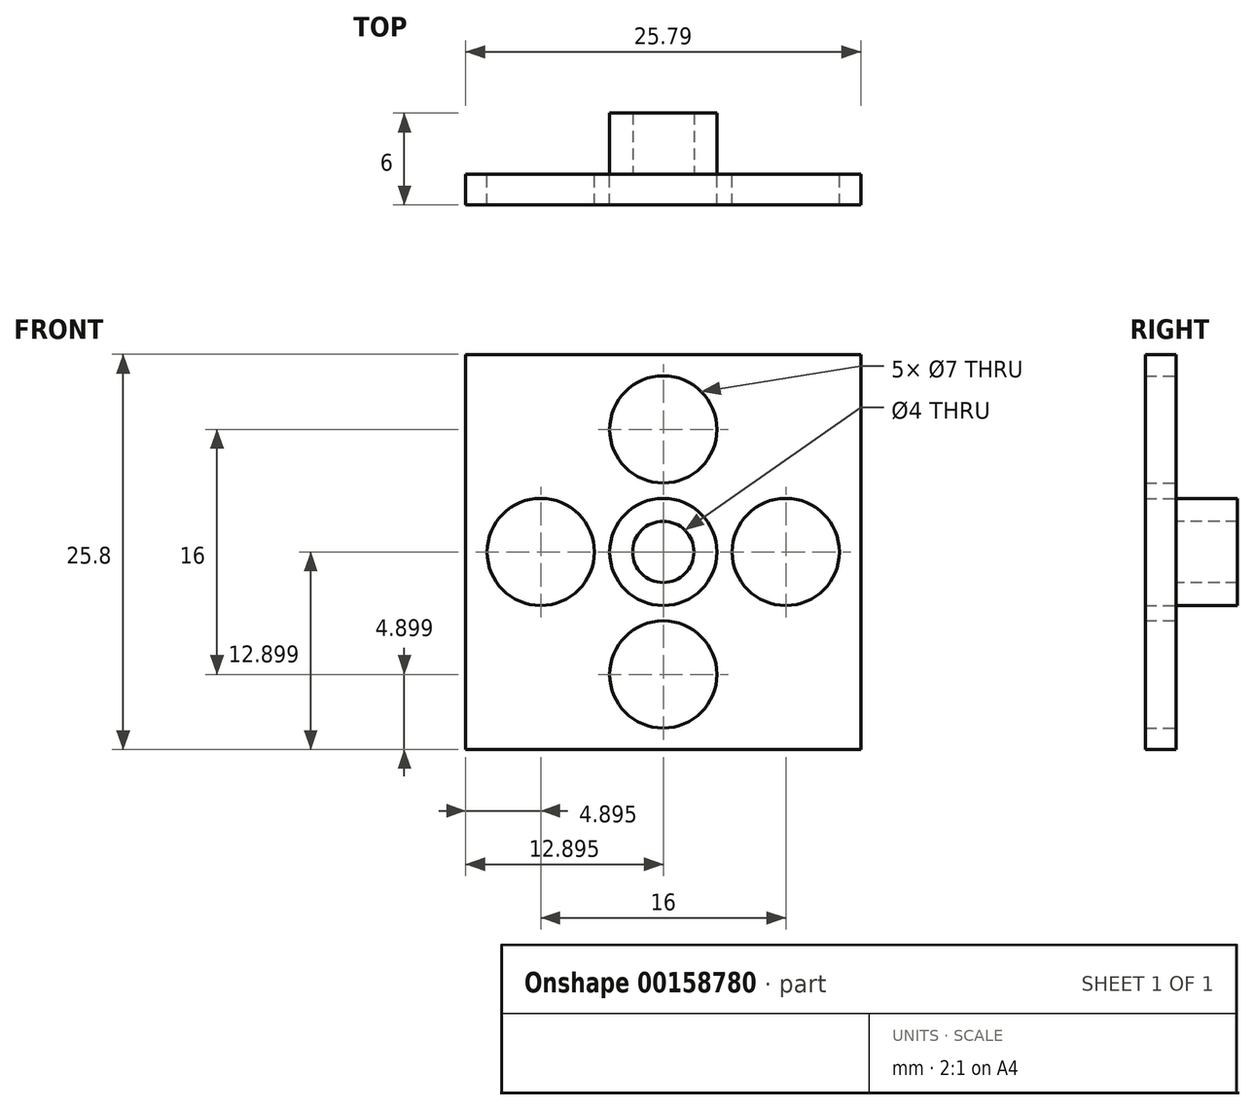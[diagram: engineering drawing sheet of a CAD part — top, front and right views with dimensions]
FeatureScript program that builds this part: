
annotation { "Feature Type Name" : "Feature", "Feature Type Description" : "" }
export const myFeature = defineFeature(function(context is Context, id is Id, definition is map)
    precondition{}
    {
        {
            var Q0;
            Q0=qCreatedBy(makeId("Front.planeOp"),FACE);
            var sketch = newSketch(context, id + "F0", { "sketchPlane" : qUnion([Q0])});
            skPoint(sketch, "E0.middle", {"position": v(0.36, -0.48) * mm});
            skLineSegment(sketch, "E1.top", {"start": v(-7.64, -8.48) * mm, "end": v(8.36, -8.48) * mm, "construction": true});
            skLineSegment(sketch, "E1.left", {"start": v(-7.64, 7.52) * mm, "end": v(-7.64, -8.48) * mm, "construction": true});
            skLineSegment(sketch, "E1.right", {"start": v(8.36, 7.52) * mm, "end": v(8.36, -8.48) * mm, "construction": true});
            skLineSegment(sketch, "E2", {"start": v(-7.64, 7.52) * mm, "end": v(8.36, 7.52) * mm, "construction": true});
            skLineSegment(sketch, "E3", {"start": v(0.36, -0.48) * mm, "end": v(-27.14, 27.02) * mm, "construction": true});
            skLineSegment(sketch, "E4", {"start": v(0.36, -0.48) * mm, "end": v(-27.14, -27.98) * mm, "construction": true});
            skLineSegment(sketch, "E5", {"start": v(0.36, -0.48) * mm, "end": v(27.86, 27.02) * mm, "construction": true});
            skLineSegment(sketch, "E6", {"start": v(0.36, -0.48) * mm, "end": v(27.86, -27.98) * mm, "construction": true});
            skLineSegment(sketch, "E7", {"start": v(0.36, -0.48) * mm, "end": v(0.36, 27.02) * mm, "construction": true});
            skLineSegment(sketch, "E8", {"start": v(0.36, -8.48) * mm, "end": v(0.36, -27.98) * mm, "construction": true});
            skPoint(sketch, "E9", {"position": v(-7.64, 7.52) * mm});
            skLineSegment(sketch, "E10", {"start": v(21.88, 21.04) * mm, "end": v(-21.17, 21.04) * mm, "construction": true});
            skLineSegment(sketch, "E11", {"start": v(-21.17, 21.04) * mm, "end": v(-21.17, -22) * mm, "construction": true});
            skLineSegment(sketch, "E12", {"start": v(-21.17, -22) * mm, "end": v(21.88, -22) * mm, "construction": true});
            skLineSegment(sketch, "E13", {"start": v(21.88, -22) * mm, "end": v(21.88, 21.04) * mm, "construction": true});
            skLineSegment(sketch, "E14", {"start": v(0.36, -0.48) * mm, "end": v(-19.04, -0.48) * mm, "construction": true});
            skLineSegment(sketch, "E15", {"start": v(-27.14, -0.48) * mm, "end": v(-19.04, -0.48) * mm, "construction": true});
            skLineSegment(sketch, "E16", {"start": v(0.36, -0.48) * mm, "end": v(27.86, -0.48) * mm, "construction": true});
            skLineSegment(sketch, "E17", {"start": v(0.36, -0.48) * mm, "end": v(0.36, -8.48) * mm, "construction": true});
            skCircle(sketch, "E18", {"center": v(8.36, -0.48) * mm, "radius": 1.5 * mm});
            skCircle(sketch, "E19", {"center": v(-7.64, -0.48) * mm, "radius": 1.5 * mm});
            skCircle(sketch, "E20", {"center": v(0.36, -8.48) * mm, "radius": 1.5 * mm});
            skLineSegment(sketch, "E21.MirrorCS", {"start": v(0.36, -0.48) * mm, "end": v(19.75, -0.48) * mm, "construction": true});
            skCircle(sketch, "E22", {"center": v(0.36, -0.48) * mm, "radius": 19.53 * mm, "construction": true});
            skLineSegment(sketch, "E23", {"start": v(0.36, 23.08) * mm, "end": v(0.36, 22.48) * mm});
            skCircle(sketch, "E24", {"center": v(0.36, -0.48) * mm, "radius": 2 * mm});
            skCircle(sketch, "E25", {"center": v(0.36, -0.48) * mm, "radius": 3.5 * mm});
            skCircle(sketch, "E26", {"center": v(0.36, -0.48) * mm, "radius": 4.9 * mm, "construction": true});
            skCircle(sketch, "E27", {"center": v(8.36, -0.48) * mm, "radius": 3.5 * mm});
            skLineSegment(sketch, "E28.bottom", {"start": v(-12.54, -13.38) * mm, "end": v(13.25, -13.38) * mm});
            skLineSegment(sketch, "E28.top", {"start": v(-12.54, 12.42) * mm, "end": v(13.25, 12.42) * mm});
            skLineSegment(sketch, "E28.left", {"start": v(-12.54, -13.38) * mm, "end": v(-12.54, 12.42) * mm});
            skLineSegment(sketch, "E28.right", {"start": v(13.25, -13.38) * mm, "end": v(13.25, 12.42) * mm});
            skCircle(sketch, "E29.MirrorC", {"center": v(-7.64, -0.48) * mm, "radius": 3.5 * mm});
            skCircle(sketch, "E30.MirrorC", {"center": v(0.36, -8.48) * mm, "radius": 3.5 * mm});
            skCircle(sketch, "E31.MirrorC", {"center": v(0.36, 7.52) * mm, "radius": 3.5 * mm});
            skSolve(sketch);
        }
        {
            var Q0;
            Q0=makeQuery(id+"F0.imprint","IMPRINT",FACE,{"disambiguationData":[TD([[makeQuery(id+"F0.imprint","IMPRINT",EDGE,{"derivedFrom":sQuery(id+"F0.wireOp",EDGE,"E24")}),-1.0]])]});
            extrude(context, id + "F1", {"entities" : qUnion([Q0]), "oppositeDirection" : true, "depth" : 4 * mm});
        }
        {
            var Q0;
            Q0=makeQuery(id+"F0.imprint","IMPRINT",FACE,{"disambiguationData":[TD([[makeQuery(id+"F0.imprint","IMPRINT",EDGE,{"derivedFrom":sQuery(id+"F0.wireOp",EDGE,"E25")}),-1.0]])]});
            var Q1;
            Q1=makeQuery(id+"F0.imprint","IMPRINT",FACE,{"disambiguationData":[TD([[makeQuery(id+"F0.imprint","IMPRINT",EDGE,{"derivedFrom":sQuery(id+"F0.wireOp",EDGE,"2a59d5c3-b0ba-4150-aeea-9719cb5647a7")}),-1.0]])]});
            extrude(context, id + "F2", {"entities" : qUnion([Q0, Q1]), "depth" : 2 * mm});
        }
        {
            var Q0;
            Q0=makeQuery(id+"F1.opExtrude","CAP_FACE",FACE,{"disambiguationData":[OSD([sQuery(id+"F0.wireOp",EDGE,"E24"),sQuery(id+"F0.wireOp",EDGE,"E25")])],"isStart":true});
            extrude(context, id + "F3", {"entities" : qUnion([Q0]), "depth" : 2 * mm});
        }
        {
            var Q0;
            Q0=makeQuery(id+"F3.opExtrude","SWEPT_BODY",BODY,{"disambiguationData":[OSD([sQuery(id+"F0.wireOp",EDGE,"E24"),sQuery(id+"F0.wireOp",EDGE,"E25")])]});
            deleteBodies(context, id + "F4", {"entities" : qUnion([Q0])});
        }
    });
